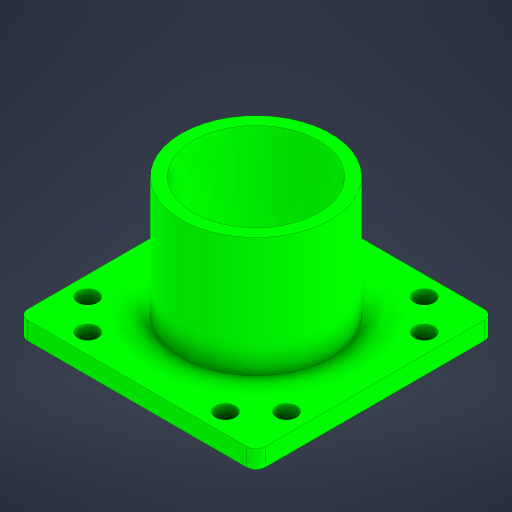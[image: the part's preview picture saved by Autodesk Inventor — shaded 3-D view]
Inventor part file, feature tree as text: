
AUTODESK INVENTOR PART (.ipt)
format: ipt  version: 2023.4 (Build 274418000, 418)  size: 248,832 bytes
history: native  units: mm
features: other x3, extrude x1, projected_geometry x1, sketch x1, reference x1
ambient origin geometry x8: Origin, YZ Plane, XZ Plane, XY Plane, X Axis, Y Axis, Z Axis, Center Point
bodies: Solid1 (feature_tree)
feature tree (7):
  extrude  "Extrusion1"  Depth=25.0mm TaperAngle=0.0deg
  projected_geometry  "Projected Loop1"
  sketch  "Sketch3"  dims[d20=3.75mm d21=0.0mm d37=25.0mm d38=0.0mm d39=2.75mm d40=50.0mm d42=4.75mm d43=10.0mm d45=10.0mm d47=25.0mm d48=0.0mm d49=2.5mm d50=2.5mm d51=0.0mm d52=26.25mm d53=2.5mm d22=0.5mm d23=0.872665mm d24=0.5mm d25=0.872665mm]
  reference  "Reference1"
  parser-record x1  (decoder bookkeeping rows leaked as tree rows — omitted from the tree; the rows remain in map.json)
  other  "Cube 1x1 V5.iam"
  other  "Cube 1x1 Top V5:1"
note: 1 file-system path scrubbed to <path> (originals preserved in map.json)
